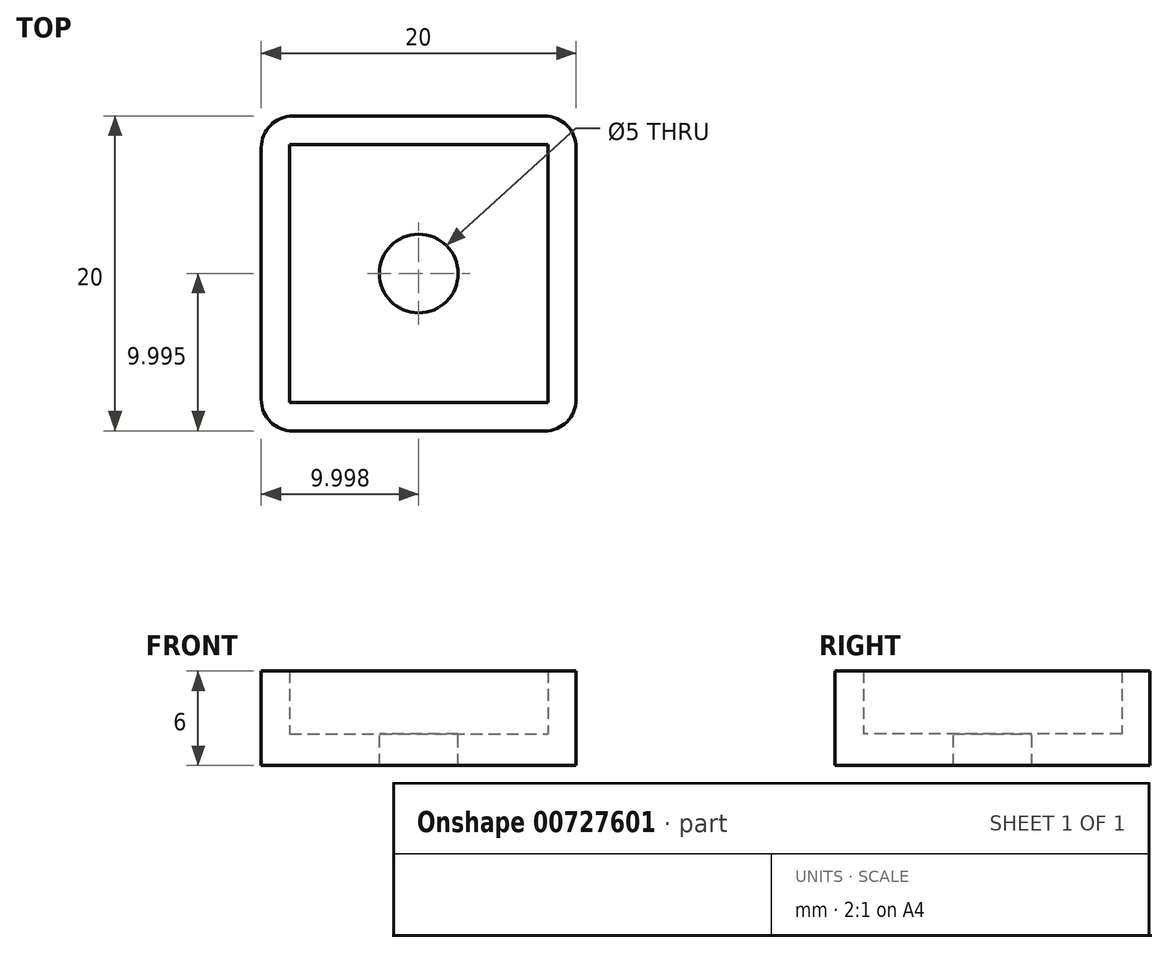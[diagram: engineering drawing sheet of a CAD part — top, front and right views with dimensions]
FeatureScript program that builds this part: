
annotation { "Feature Type Name" : "Feature", "Feature Type Description" : "" }
export const myFeature = defineFeature(function(context is Context, id is Id, definition is map)
    precondition{}
    {
        {
            var Q0;
            Q0=qCreatedBy(makeId("Top.planeOp"),FACE);
            var sketch = newSketch(context, id + "F0", { "sketchPlane" : qUnion([Q0])});
            skLineSegment(sketch, "E0.bottom", {"start": v(-31.78, 12.23) * mm, "end": v(-15.78, 12.23) * mm});
            skLineSegment(sketch, "E0.top", {"start": v(-31.78, -7.77) * mm, "end": v(-15.78, -7.77) * mm});
            skLineSegment(sketch, "E0.left", {"start": v(-33.78, 10.23) * mm, "end": v(-33.78, -5.77) * mm});
            skLineSegment(sketch, "E0.right", {"start": v(-13.78, 10.23) * mm, "end": v(-13.78, -5.77) * mm});
            skPoint(sketch, "E1.visualSharp", {"position": v(-33.78, 12.23) * mm});
            skArc(sketch, "E1.filletArc", {"start": v(-31.78, 12.23) * mm, "mid": v(-33.2, 11.64) * mm, "end": v(-33.78, 10.23) * mm});
            skPoint(sketch, "E2.visualSharp", {"position": v(-13.78, 12.23) * mm});
            skArc(sketch, "E2.filletArc", {"start": v(-13.78, 10.23) * mm, "mid": v(-14.37, 11.64) * mm, "end": v(-15.78, 12.23) * mm});
            skPoint(sketch, "E3.visualSharp", {"position": v(-13.78, -7.77) * mm});
            skArc(sketch, "E3.filletArc", {"start": v(-15.78, -7.77) * mm, "mid": v(-14.37, -7.19) * mm, "end": v(-13.78, -5.77) * mm});
            skPoint(sketch, "E4.visualSharp", {"position": v(-33.78, -7.77) * mm});
            skArc(sketch, "E4.filletArc", {"start": v(-33.78, -5.77) * mm, "mid": v(-33.2, -7.19) * mm, "end": v(-31.78, -7.77) * mm});
            skSolve(sketch);
        }
        {
            var Q0;
            Q0 = qSketchRegion(id + "F0", true);
            extrude(context, id + "F1", {"entities" : qUnion([Q0]), "depth" : 2 * mm, "offsetDistance" : 25 * mm});
        }
        {
            var Q0;
            Q0=makeQuery(id+"F1.opExtrude","CAP_FACE",FACE,{"disambiguationData":[OSD([sQuery(id+"F0.wireOp",EDGE,"E0.bottom"),sQuery(id+"F0.wireOp",EDGE,"E0.top"),sQuery(id+"F0.wireOp",EDGE,"E0.left"),sQuery(id+"F0.wireOp",EDGE,"E0.right"),sQuery(id+"F0.wireOp",EDGE,"E1.filletArc"),sQuery(id+"F0.wireOp",EDGE,"E2.filletArc"),sQuery(id+"F0.wireOp",EDGE,"E3.filletArc"),sQuery(id+"F0.wireOp",EDGE,"E4.filletArc")])],"isStart":false});
            var sketch = newSketch(context, id + "F2", { "sketchPlane" : qUnion([Q0])});
            skLineSegment(sketch, "E5.0", {"start": v(-31.98, 10.43) * mm, "end": v(-15.58, 10.43) * mm});
            skLineSegment(sketch, "E5.1", {"start": v(-31.98, 10.43) * mm, "end": v(-31.98, -5.97) * mm});
            skLineSegment(sketch, "E5.2", {"start": v(-31.98, -5.97) * mm, "end": v(-15.58, -5.97) * mm});
            skLineSegment(sketch, "E5.3", {"start": v(-15.58, 10.43) * mm, "end": v(-15.58, -5.97) * mm});
            skSolve(sketch);
        }
        {
            var Q0;
            Q0=makeQuery(id+"F2.imprint","IMPRINT",FACE,{"disambiguationData":[TD([[makeQuery(id+"F2.imprint","IMPRINT",EDGE,{"derivedFrom":sQuery(id+"F2.wireOp",EDGE,"E5.0")}),1.0]])]});
            extrude(context, id + "F3", {"entities" : qUnion([Q0]), "operationType" : NewBodyOperationType.ADD, "depth" : 4 * mm, "offsetDistance" : 25 * mm});
        }
        {
            var Q0;
            Q0=makeQuery(id+"F1.opExtrude","CAP_FACE",FACE,{"disambiguationData":[OSD([sQuery(id+"F0.wireOp",EDGE,"E0.bottom"),sQuery(id+"F0.wireOp",EDGE,"E0.top"),sQuery(id+"F0.wireOp",EDGE,"E0.left"),sQuery(id+"F0.wireOp",EDGE,"E0.right"),sQuery(id+"F0.wireOp",EDGE,"E1.filletArc"),sQuery(id+"F0.wireOp",EDGE,"E2.filletArc"),sQuery(id+"F0.wireOp",EDGE,"E3.filletArc"),sQuery(id+"F0.wireOp",EDGE,"E4.filletArc")])],"isStart":false});
            var sketch = newSketch(context, id + "F4", { "sketchPlane" : qUnion([Q0])});
            skCircle(sketch, "E6", {"center": v(-23.78, 2.23) * mm, "radius": 2.5 * mm});
            skSolve(sketch);
        }
        {
            var Q0;
            Q0=makeQuery(id+"F4.imprint","IMPRINT",FACE,{"disambiguationData":[TD([[makeQuery(id+"F4.imprint","IMPRINT",EDGE,{"derivedFrom":sQuery(id+"F4.wireOp",EDGE,"E6")}),1.0]])]});
            extrude(context, id + "F5", {"entities" : qUnion([Q0]), "operationType" : NewBodyOperationType.REMOVE, "oppositeDirection" : true, "depth" : 25 * mm, "offsetDistance" : 25 * mm});
        }
    });
